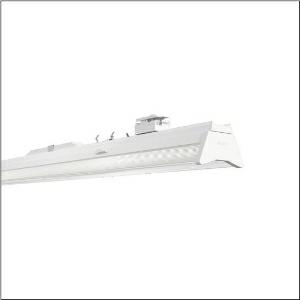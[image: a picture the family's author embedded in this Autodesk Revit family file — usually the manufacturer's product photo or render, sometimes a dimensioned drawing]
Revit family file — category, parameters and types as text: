
# Revit family: licross_r__11_performance_mo_51tm167n485g_4c90
name_source: partatom
category: Lighting Fixtures
units: mm (PartAtom-declared; Revit-internal decimal feet)

## family parameters
Cut with Voids When Loaded = No
Host = Face
Light Source = No
Part Type = Normal
Room Calculation Point = No
Round Connector Dimension = Use Diameter
Shared = No

## types (1)
- Licross® 11 Performance MO (1 x LED, 8840 lm, 48.6 W, 4000K)
    Apparent Load = 49 VA
    CIE Flux Codes = 66 88 96 79 100
    Color Rendering = 80
    Color Temperature = 4000K
    Default Elevation = 1800 mm
    Description = Licross® 11 Performance MO, luminaire insert, of sheet steel, galvanised, coil coated, white, length: 1.500mm, width: 120mm, height: 123mm, LED rated luminous flux: 8.840lm, light colour: 840, control gear: ON/OFF, with plug, 3-pole, with phase selection, mains connection: 220..240V, AC, 50/60Hz, rated input power: 49W, internal wiring halogen-free, primary light control with lens, of plastic, primary optical cover: cover, of PMMA, light emission: direct/indirect distribution, primary light characteristic: symmetric, protection rating (complete): IP40, insulation class (complete): insulation class I (protective earthing), certification: CE, ENEC, VDE, UKCA, protection symbol: D if used in an environment without relevant dust loads with corresponding accessories, impact resistance: IK06, permissible ambient temperature for indoor applications: -25..+35°C, corresponds to IFS (International Featured Standards) requirements for safety and quality in the food industry, reducing of maximum allowable ambient temperature of 5°C with ceiling mounting, LABS conformity tested according to VDMA 24364:2018-05, packaging unit: 1 piece
    Height = 114 mm
    Lamp = 1 x LED
    Lamp Light Flux = 8840 lm
    Lamp Power = 48.6 W
    Lamp count = 1
    Length = 1500 mm
    Luminous efficacy = 182 lm/W
    Manufacturer = Siteco
    ModVariant = No
    Model = 51TM167N485G
    Mounting Place = Ceiling
    Mounting Type = Pendant
    Number of Poles = 1
    OnlyDefault = Yes
    Power Factor = 1
    Product Name = Licross® 11 Performance MO
    Product group = luminaire insert | ceiling pendant
    ProductGroupID = 902
    Protection Class = Protection class I
    Protection Degree = IP 40
    RLX_Detail_Level = 1
    RLX_Emergency_Light_Flux = 0 lm
    RLX_Emergency_Type = 0
    RLX_Emergency_Type_DB = No
    RlxData = <blob elided: 30441 chars, md5=d8698d04>
    Socket = socket
    Standby Power = 0 W
    System Light Flux = 8840 lm
    System Power = 49 W
    Type Comments = Product without accessories
    Type Image = l_1256138.jpg
    URL = http://relux.com
    VarID = ---
    Voltage = 0 V
    Weight = 0.00 kg
    Width = 120 mm

## geometry (parser evidence)
native form markers: Blend x4, Sweep x10
no freeform markers — native parametric forms only
